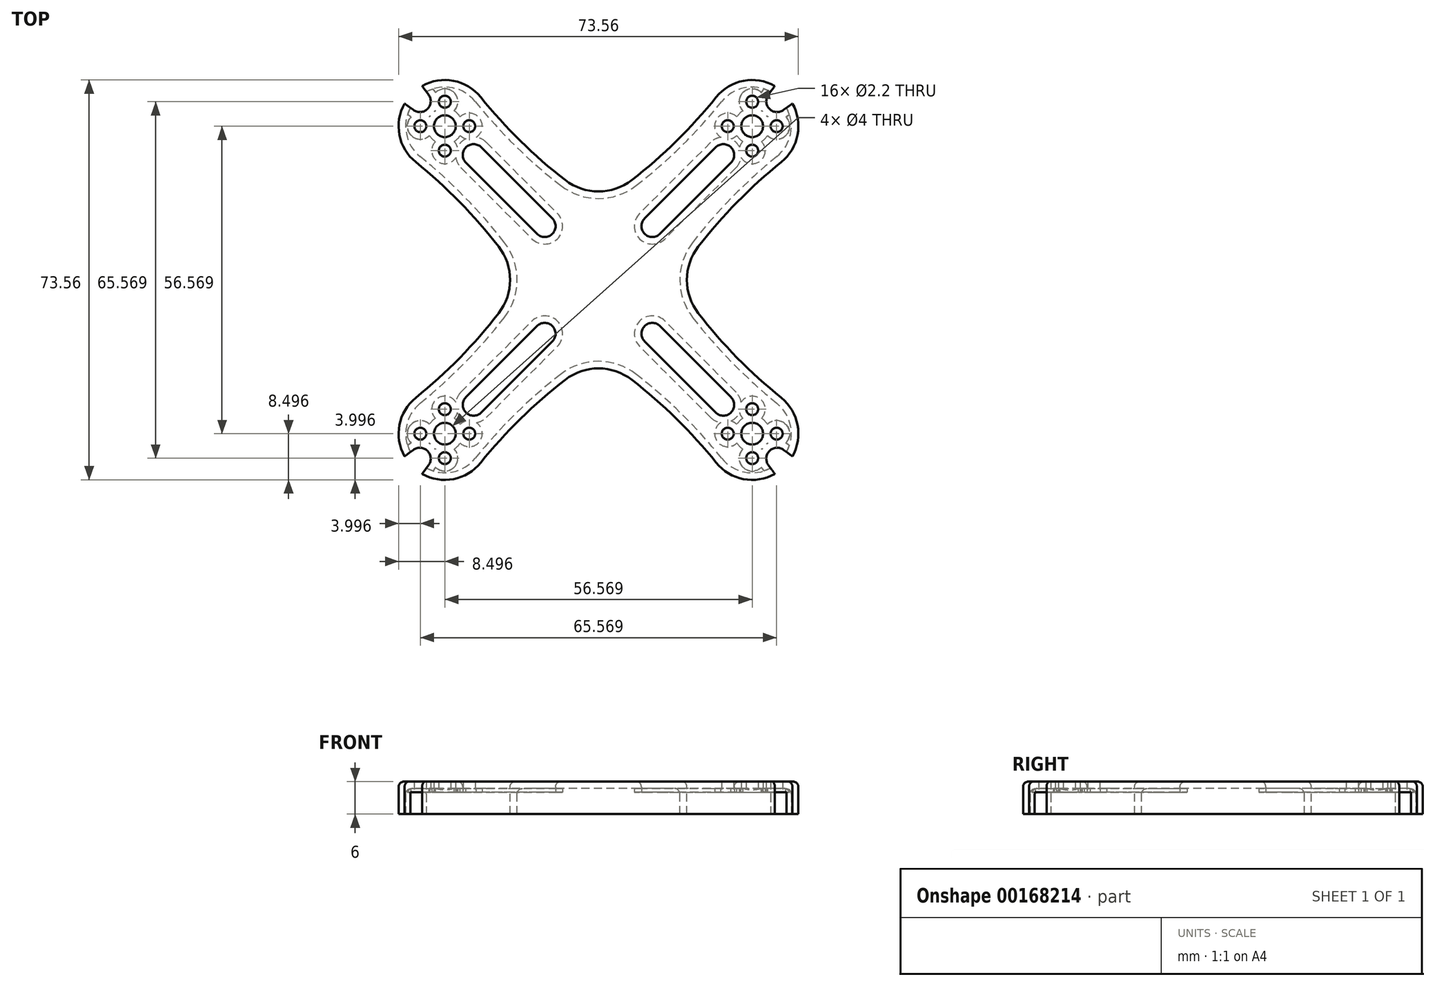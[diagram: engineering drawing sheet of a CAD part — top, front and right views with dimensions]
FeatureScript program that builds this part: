
annotation { "Feature Type Name" : "Feature", "Feature Type Description" : "" }
export const myFeature = defineFeature(function(context is Context, id is Id, definition is map)
    precondition{}
    {
        {
            var Q0;
            Q0=qCreatedBy(makeId("Top.planeOp"),FACE);
            var sketch = newSketch(context, id + "F0", { "sketchPlane" : qUnion([Q0])});
            skCircle(sketch, "E0", {"center": v(0, 0) * mm, "radius": 40 * mm, "construction": true});
            skLineSegment(sketch, "E1", {"start": v(0, 0) * mm, "end": v(-34.3, 34.3) * mm, "construction": true});
            skCircle(sketch, "E2", {"center": v(-28.28, 28.28) * mm, "radius": 2 * mm});
            skLineSegment(sketch, "E3", {"start": v(-28.28, 28.28) * mm, "end": v(-23.78, 28.28) * mm, "construction": true});
            skCircle(sketch, "E4", {"center": v(-23.78, 28.28) * mm, "radius": 1.1 * mm});
            skCircle(sketch, "E5.1.0", {"center": v(-28.28, 32.78) * mm, "radius": 1.1 * mm});
            skCircle(sketch, "E5.2.0", {"center": v(-32.78, 28.28) * mm, "radius": 1.1 * mm});
            skCircle(sketch, "E5.3.0", {"center": v(-28.28, 23.78) * mm, "radius": 1.1 * mm});
            skCircle(sketch, "E6", {"center": v(-28.28, 28.28) * mm, "radius": 7.5 * mm, "construction": true});
            skArc(sketch, "E7", {"start": v(-21.67, 33.62) * mm, "mid": v(-26.68, 36.63) * mm, "end": v(-32.46, 35.7) * mm});
            skCircle(sketch, "E8", {"center": v(-28.28, 28.28) * mm, "radius": 6.5 * mm, "construction": true});
            skCircle(sketch, "E9", {"center": v(0, 0) * mm, "radius": 6.5 * mm});
            skLineSegment(sketch, "E10", {"start": v(-28.28, 28.28) * mm, "end": v(-26.87, 29.7) * mm, "construction": true});
            skLineSegment(sketch, "E11", {"start": v(-23.69, 32.88) * mm, "end": v(4.6, 4.6) * mm, "construction": true});
            skLineSegment(sketch, "E12.MirrorCS", {"start": v(-32.88, 23.69) * mm, "end": v(-4.6, -4.6) * mm, "construction": true});
            skCircle(sketch, "E13", {"center": v(-28.28, 28.28) * mm, "radius": 26 * mm, "construction": true});
            skCircle(sketch, "E14", {"center": v(0, 0) * mm, "radius": 14 * mm});
            skArc(sketch, "E15", {"start": v(-21.67, 33.62) * mm, "mid": v(-11.6, 22.96) * mm, "end": v(0, 14) * mm});
            skArc(sketch, "E16.MirrorCS", {"start": v(-33.62, 21.67) * mm, "mid": v(-22.96, 11.6) * mm, "end": v(-14, 0) * mm});
            skLineSegment(sketch, "E17", {"start": v(-22.98, 22.98) * mm, "end": v(-9.9, 9.9) * mm});
            skArc(sketch, "E18.0.startCap", {"start": v(-24.4, 21.57) * mm, "mid": v(-24.4, 24.4) * mm, "end": v(-21.57, 24.4) * mm});
            skArc(sketch, "E18.0.endCap", {"start": v(-8.49, 11.31) * mm, "mid": v(-8.49, 8.49) * mm, "end": v(-11.31, 8.49) * mm});
            skLineSegment(sketch, "E18.0.left", {"start": v(-21.57, 24.4) * mm, "end": v(-8.49, 11.31) * mm});
            skLineSegment(sketch, "E18.0.right", {"start": v(-24.4, 21.57) * mm, "end": v(-11.31, 8.49) * mm});
            skArc(sketch, "E19", {"start": v(-34.06, 31.27) * mm, "mid": v(-31.47, 31.47) * mm, "end": v(-31.27, 34.06) * mm});
            skLineSegment(sketch, "E20", {"start": v(-31.27, 34.06) * mm, "end": v(-32.46, 35.7) * mm});
            skLineSegment(sketch, "E21.MirrorCS", {"start": v(-34.06, 31.27) * mm, "end": v(-35.7, 32.46) * mm});
            skArc(sketch, "E22.trimOffspring", {"start": v(-35.7, 32.46) * mm, "mid": v(-36.63, 26.68) * mm, "end": v(-33.62, 21.67) * mm});
            skLineSegment(sketch, "E23", {"start": v(0, 0) * mm, "end": v(0, 14) * mm});
            skLineSegment(sketch, "E24", {"start": v(0, 0) * mm, "end": v(-14, 0) * mm});
            skSolve(sketch);
        }
        {
            var Q0;
            {var subQ0=sQuery(id+"F0.wireOp",EDGE,"E23");var subQ1=sQuery(id+"F0.wireOp",EDGE,"E9");var subQ2=makeQuery(id+"F0.imprint","INTERSECT",VERTEX,{"derivedFrom":[subQ1,subQ0]});Q0=makeQuery(id+"F0.imprint","IMPRINT",FACE,{"disambiguationData":[TD([[makeQuery(id+"F0.imprint","IMPRINT",EDGE,{"disambiguationData":[TD([[subQ2,-1.0]])],"derivedFrom":subQ1}),1.0]])]});}
            var Q1;
            Q1=makeQuery(id+"F0.imprint","IMPRINT",FACE,{"disambiguationData":[TD([[makeQuery(id+"F0.imprint","IMPRINT",EDGE,{"derivedFrom":sQuery(id+"F0.wireOp",EDGE,"E2")}),-1.0]])]});
            var Q2;
            {var subQ4=sQuery(id+"F0.wireOp",EDGE,"E23");var subQ5=sQuery(id+"F0.wireOp",EDGE,"E9");var subQ6=makeQuery(id+"F0.imprint","INTERSECT",VERTEX,{"derivedFrom":[subQ5,subQ4]});Q2=makeQuery(id+"F0.imprint","IMPRINT",FACE,{"disambiguationData":[TD([[makeQuery(id+"F0.imprint","IMPRINT",EDGE,{"disambiguationData":[TD([[subQ6,-1.0]])],"derivedFrom":subQ5}),-1.0]])]});}
            extrude(context, id + "F1", {"entities" : qUnion([Q0, Q1, Q2]), "depth" : 6 * mm});
        }
        {
            var Q0;
            Q0=makeQuery(id+"F1.opExtrude","SWEPT_BODY",BODY,{"disambiguationData":[OSD([sQuery(id+"F0.wireOp",EDGE,"E2"),sQuery(id+"F0.wireOp",EDGE,"E4"),sQuery(id+"F0.wireOp",EDGE,"E5.1.0"),sQuery(id+"F0.wireOp",EDGE,"E5.2.0"),sQuery(id+"F0.wireOp",EDGE,"E5.3.0"),sQuery(id+"F0.wireOp",EDGE,"E7"),sQuery(id+"F0.wireOp",EDGE,"E15"),sQuery(id+"F0.wireOp",EDGE,"E16.MirrorCS"),sQuery(id+"F0.wireOp",EDGE,"E18.0.startCap"),sQuery(id+"F0.wireOp",EDGE,"E18.0.endCap"),sQuery(id+"F0.wireOp",EDGE,"E18.0.left"),sQuery(id+"F0.wireOp",EDGE,"E18.0.right"),sQuery(id+"F0.wireOp",EDGE,"E19"),sQuery(id+"F0.wireOp",EDGE,"E20"),sQuery(id+"F0.wireOp",EDGE,"E21.MirrorCS"),sQuery(id+"F0.wireOp",EDGE,"E22.trimOffspring"),sQuery(id+"F0.wireOp",EDGE,"E23"),sQuery(id+"F0.wireOp",EDGE,"E24")])]});
            var Q1;
            Q1=makeQuery(id+"F1.opExtrude","SWEPT_EDGE",EDGE,{"disambiguationData":[OSD([sQuery(id+"F0.wireOp",EDGE,"E23"),sQuery(id+"F0.wireOp",EDGE,"E24")])]});
            circularPattern(context, id + "F2", {"entities" : qUnion([Q0]), "axis" : qUnion([Q1]), "angle" : 360 * degree, "instanceCount" : 4, "equalSpace" : true});
        }
        {
            var Q0;
            Q0=makeQuery(id+"F1.opExtrude","SWEPT_BODY",BODY,{"disambiguationData":[OSD([sQuery(id+"F0.wireOp",EDGE,"E2"),sQuery(id+"F0.wireOp",EDGE,"E4"),sQuery(id+"F0.wireOp",EDGE,"E5.1.0"),sQuery(id+"F0.wireOp",EDGE,"E5.2.0"),sQuery(id+"F0.wireOp",EDGE,"E5.3.0"),sQuery(id+"F0.wireOp",EDGE,"E7"),sQuery(id+"F0.wireOp",EDGE,"E15"),sQuery(id+"F0.wireOp",EDGE,"E16.MirrorCS"),sQuery(id+"F0.wireOp",EDGE,"E18.0.startCap"),sQuery(id+"F0.wireOp",EDGE,"E18.0.endCap"),sQuery(id+"F0.wireOp",EDGE,"E18.0.left"),sQuery(id+"F0.wireOp",EDGE,"E18.0.right"),sQuery(id+"F0.wireOp",EDGE,"E19"),sQuery(id+"F0.wireOp",EDGE,"E20"),sQuery(id+"F0.wireOp",EDGE,"E21.MirrorCS"),sQuery(id+"F0.wireOp",EDGE,"E22.trimOffspring"),sQuery(id+"F0.wireOp",EDGE,"E23"),sQuery(id+"F0.wireOp",EDGE,"E24")])]});
            var Q1;
            Q1=makeQuery(id+"F2.opPattern","COPY",BODY,{"derivedFrom":makeQuery(id+"F1.opExtrude","SWEPT_BODY",BODY,{"disambiguationData":[OSD([sQuery(id+"F0.wireOp",EDGE,"E2"),sQuery(id+"F0.wireOp",EDGE,"E4"),sQuery(id+"F0.wireOp",EDGE,"E5.1.0"),sQuery(id+"F0.wireOp",EDGE,"E5.2.0"),sQuery(id+"F0.wireOp",EDGE,"E5.3.0"),sQuery(id+"F0.wireOp",EDGE,"E7"),sQuery(id+"F0.wireOp",EDGE,"E15"),sQuery(id+"F0.wireOp",EDGE,"E16.MirrorCS"),sQuery(id+"F0.wireOp",EDGE,"E18.0.startCap"),sQuery(id+"F0.wireOp",EDGE,"E18.0.endCap"),sQuery(id+"F0.wireOp",EDGE,"E18.0.left"),sQuery(id+"F0.wireOp",EDGE,"E18.0.right"),sQuery(id+"F0.wireOp",EDGE,"E19"),sQuery(id+"F0.wireOp",EDGE,"E20"),sQuery(id+"F0.wireOp",EDGE,"E21.MirrorCS"),sQuery(id+"F0.wireOp",EDGE,"E22.trimOffspring"),sQuery(id+"F0.wireOp",EDGE,"E23"),sQuery(id+"F0.wireOp",EDGE,"E24")])]}),"instanceName":"1"});
            var Q2;
            Q2=makeQuery(id+"F2.opPattern","COPY",BODY,{"derivedFrom":makeQuery(id+"F1.opExtrude","SWEPT_BODY",BODY,{"disambiguationData":[OSD([sQuery(id+"F0.wireOp",EDGE,"E2"),sQuery(id+"F0.wireOp",EDGE,"E4"),sQuery(id+"F0.wireOp",EDGE,"E5.1.0"),sQuery(id+"F0.wireOp",EDGE,"E5.2.0"),sQuery(id+"F0.wireOp",EDGE,"E5.3.0"),sQuery(id+"F0.wireOp",EDGE,"E7"),sQuery(id+"F0.wireOp",EDGE,"E15"),sQuery(id+"F0.wireOp",EDGE,"E16.MirrorCS"),sQuery(id+"F0.wireOp",EDGE,"E18.0.startCap"),sQuery(id+"F0.wireOp",EDGE,"E18.0.endCap"),sQuery(id+"F0.wireOp",EDGE,"E18.0.left"),sQuery(id+"F0.wireOp",EDGE,"E18.0.right"),sQuery(id+"F0.wireOp",EDGE,"E19"),sQuery(id+"F0.wireOp",EDGE,"E20"),sQuery(id+"F0.wireOp",EDGE,"E21.MirrorCS"),sQuery(id+"F0.wireOp",EDGE,"E22.trimOffspring"),sQuery(id+"F0.wireOp",EDGE,"E23"),sQuery(id+"F0.wireOp",EDGE,"E24")])]}),"instanceName":"2"});
            var Q3;
            Q3=makeQuery(id+"F2.opPattern","COPY",BODY,{"derivedFrom":makeQuery(id+"F1.opExtrude","SWEPT_BODY",BODY,{"disambiguationData":[OSD([sQuery(id+"F0.wireOp",EDGE,"E2"),sQuery(id+"F0.wireOp",EDGE,"E4"),sQuery(id+"F0.wireOp",EDGE,"E5.1.0"),sQuery(id+"F0.wireOp",EDGE,"E5.2.0"),sQuery(id+"F0.wireOp",EDGE,"E5.3.0"),sQuery(id+"F0.wireOp",EDGE,"E7"),sQuery(id+"F0.wireOp",EDGE,"E15"),sQuery(id+"F0.wireOp",EDGE,"E16.MirrorCS"),sQuery(id+"F0.wireOp",EDGE,"E18.0.startCap"),sQuery(id+"F0.wireOp",EDGE,"E18.0.endCap"),sQuery(id+"F0.wireOp",EDGE,"E18.0.left"),sQuery(id+"F0.wireOp",EDGE,"E18.0.right"),sQuery(id+"F0.wireOp",EDGE,"E19"),sQuery(id+"F0.wireOp",EDGE,"E20"),sQuery(id+"F0.wireOp",EDGE,"E21.MirrorCS"),sQuery(id+"F0.wireOp",EDGE,"E22.trimOffspring"),sQuery(id+"F0.wireOp",EDGE,"E23"),sQuery(id+"F0.wireOp",EDGE,"E24")])]}),"instanceName":"3"});
            booleanBodies(context, id + "F3", {"operationType" : BooleanOperationType.UNION, "tools" : qUnion([Q0, Q1, Q2, Q3])});
        }
        {
            var Q0;
            {var subQ0=sQuery(id+"F0.wireOp",EDGE,"E14");Q0=makeQuery(id+"F3.opBoolean","MERGE",EDGE,{"derivedFrom":[makeQuery(id+"F2.opPattern","COPY",EDGE,{"derivedFrom":makeQuery(id+"F1.opExtrude","SWEPT_EDGE",EDGE,{"disambiguationData":[OSD([subQ0,sQuery(id+"F0.wireOp",EDGE,"E15"),sQuery(id+"F0.wireOp",EDGE,"E23")])]}),"instanceName":"2"}),makeQuery(id+"F2.opPattern","COPY",EDGE,{"derivedFrom":makeQuery(id+"F1.opExtrude","SWEPT_EDGE",EDGE,{"disambiguationData":[OSD([subQ0,sQuery(id+"F0.wireOp",EDGE,"E16.MirrorCS"),sQuery(id+"F0.wireOp",EDGE,"E24")])]}),"instanceName":"3"})]});}
            var Q1;
            {var subQ0=sQuery(id+"F0.wireOp",EDGE,"E14");Q1=makeQuery(id+"F3.opBoolean","MERGE",EDGE,{"derivedFrom":[makeQuery(id+"F1.opExtrude","SWEPT_EDGE",EDGE,{"disambiguationData":[OSD([subQ0,sQuery(id+"F0.wireOp",EDGE,"E16.MirrorCS"),sQuery(id+"F0.wireOp",EDGE,"E24")])]}),makeQuery(id+"F2.opPattern","COPY",EDGE,{"derivedFrom":makeQuery(id+"F1.opExtrude","SWEPT_EDGE",EDGE,{"disambiguationData":[OSD([subQ0,sQuery(id+"F0.wireOp",EDGE,"E15"),sQuery(id+"F0.wireOp",EDGE,"E23")])]}),"instanceName":"3"})]});}
            var Q2;
            {var subQ0=sQuery(id+"F0.wireOp",EDGE,"E14");Q2=makeQuery(id+"F3.opBoolean","MERGE",EDGE,{"derivedFrom":[makeQuery(id+"F1.opExtrude","SWEPT_EDGE",EDGE,{"disambiguationData":[OSD([subQ0,sQuery(id+"F0.wireOp",EDGE,"E15"),sQuery(id+"F0.wireOp",EDGE,"E23")])]}),makeQuery(id+"F2.opPattern","COPY",EDGE,{"derivedFrom":makeQuery(id+"F1.opExtrude","SWEPT_EDGE",EDGE,{"disambiguationData":[OSD([subQ0,sQuery(id+"F0.wireOp",EDGE,"E16.MirrorCS"),sQuery(id+"F0.wireOp",EDGE,"E24")])]}),"instanceName":"1"})]});}
            var Q3;
            {var subQ0=sQuery(id+"F0.wireOp",EDGE,"E14");Q3=makeQuery(id+"F3.opBoolean","MERGE",EDGE,{"derivedFrom":[makeQuery(id+"F2.opPattern","COPY",EDGE,{"derivedFrom":makeQuery(id+"F1.opExtrude","SWEPT_EDGE",EDGE,{"disambiguationData":[OSD([subQ0,sQuery(id+"F0.wireOp",EDGE,"E15"),sQuery(id+"F0.wireOp",EDGE,"E23")])]}),"instanceName":"1"}),makeQuery(id+"F2.opPattern","COPY",EDGE,{"derivedFrom":makeQuery(id+"F1.opExtrude","SWEPT_EDGE",EDGE,{"disambiguationData":[OSD([subQ0,sQuery(id+"F0.wireOp",EDGE,"E16.MirrorCS"),sQuery(id+"F0.wireOp",EDGE,"E24")])]}),"instanceName":"2"})]});}
            fillet(context, id + "F4", {"entities" : qUnion([Q0, Q1, Q2, Q3]), "radius" : 10 * mm, "tangentPropagation" : true, "allowEdgeOverflow" : false});
        }
        {
            var Q0;
            {var subQ0=makeQuery(id+"F1.opExtrude","CAP_FACE",FACE,{"disambiguationData":[OSD([sQuery(id+"F0.wireOp",EDGE,"E2"),sQuery(id+"F0.wireOp",EDGE,"E4"),sQuery(id+"F0.wireOp",EDGE,"E5.1.0"),sQuery(id+"F0.wireOp",EDGE,"E5.2.0"),sQuery(id+"F0.wireOp",EDGE,"E5.3.0"),sQuery(id+"F0.wireOp",EDGE,"E7"),sQuery(id+"F0.wireOp",EDGE,"E15"),sQuery(id+"F0.wireOp",EDGE,"E16.MirrorCS"),sQuery(id+"F0.wireOp",EDGE,"E18.0.startCap"),sQuery(id+"F0.wireOp",EDGE,"E18.0.endCap"),sQuery(id+"F0.wireOp",EDGE,"E18.0.left"),sQuery(id+"F0.wireOp",EDGE,"E18.0.right"),sQuery(id+"F0.wireOp",EDGE,"E19"),sQuery(id+"F0.wireOp",EDGE,"E20"),sQuery(id+"F0.wireOp",EDGE,"E21.MirrorCS"),sQuery(id+"F0.wireOp",EDGE,"E22.trimOffspring"),sQuery(id+"F0.wireOp",EDGE,"E23"),sQuery(id+"F0.wireOp",EDGE,"E24")])],"isStart":true});Q0=makeQuery(id+"F3.opBoolean","MERGE",FACE,{"derivedFrom":[subQ0,makeQuery(id+"F2.opPattern","COPY",FACE,{"derivedFrom":subQ0,"instanceName":"1"}),makeQuery(id+"F2.opPattern","COPY",FACE,{"derivedFrom":subQ0,"instanceName":"2"}),makeQuery(id+"F2.opPattern","COPY",FACE,{"derivedFrom":subQ0,"instanceName":"3"})]});}
            shell(context, id + "F5", {"entities" : qUnion([Q0]), "thickness" : 1.3 * mm});
        }
        {
            var Q0;
            {var subQ0=makeQuery(id+"F1.opExtrude","CAP_FACE",FACE,{"disambiguationData":[OSD([sQuery(id+"F0.wireOp",EDGE,"E2"),sQuery(id+"F0.wireOp",EDGE,"E4"),sQuery(id+"F0.wireOp",EDGE,"E5.1.0"),sQuery(id+"F0.wireOp",EDGE,"E5.2.0"),sQuery(id+"F0.wireOp",EDGE,"E5.3.0"),sQuery(id+"F0.wireOp",EDGE,"E7"),sQuery(id+"F0.wireOp",EDGE,"E15"),sQuery(id+"F0.wireOp",EDGE,"E16.MirrorCS"),sQuery(id+"F0.wireOp",EDGE,"E18.0.startCap"),sQuery(id+"F0.wireOp",EDGE,"E18.0.endCap"),sQuery(id+"F0.wireOp",EDGE,"E18.0.left"),sQuery(id+"F0.wireOp",EDGE,"E18.0.right"),sQuery(id+"F0.wireOp",EDGE,"E19"),sQuery(id+"F0.wireOp",EDGE,"E20"),sQuery(id+"F0.wireOp",EDGE,"E21.MirrorCS"),sQuery(id+"F0.wireOp",EDGE,"E22.trimOffspring"),sQuery(id+"F0.wireOp",EDGE,"E23"),sQuery(id+"F0.wireOp",EDGE,"E24")])],"isStart":true});Q0=makeQuery(id+"F3.opBoolean","MERGE",FACE,{"derivedFrom":[subQ0,makeQuery(id+"F2.opPattern","COPY",FACE,{"derivedFrom":subQ0,"instanceName":"1"}),makeQuery(id+"F2.opPattern","COPY",FACE,{"derivedFrom":subQ0,"instanceName":"2"}),makeQuery(id+"F2.opPattern","COPY",FACE,{"derivedFrom":subQ0,"instanceName":"3"})]});}
            var sketch = newSketch(context, id + "F6", { "sketchPlane" : qUnion([Q0])});
            skPoint(sketch, "E25.0", {"position": v(21.5, 25.93) * mm});
            skLineSegment(sketch, "E26.0", {"start": v(25.31, 20.65) * mm, "end": v(12.23, 7.57) * mm});
            skArc(sketch, "E27.0", {"start": v(25.31, 20.65) * mm, "mid": v(25.93, 21.5) * mm, "end": v(26.25, 22.51) * mm});
            skArc(sketch, "E28.0", {"start": v(30, 25.46) * mm, "mid": v(29.77, 21.9) * mm, "end": v(26.25, 22.51) * mm});
            skArc(sketch, "E29.0", {"start": v(22.51, 26.25) * mm, "mid": v(21.5, 25.93) * mm, "end": v(20.65, 25.31) * mm});
            skLineSegment(sketch, "E30.0", {"start": v(20.65, 25.31) * mm, "end": v(7.57, 12.23) * mm});
            skArc(sketch, "E31.0", {"start": v(7.57, 12.23) * mm, "mid": v(7.57, 7.57) * mm, "end": v(12.23, 7.57) * mm});
            skArc(sketch, "E32.0", {"start": v(22.51, 26.25) * mm, "mid": v(21.9, 29.77) * mm, "end": v(25.46, 30) * mm});
            skArc(sketch, "E33.0", {"start": v(26.57, 31.1) * mm, "mid": v(26.6, 34.5) * mm, "end": v(29.99, 34.47) * mm});
            skArc(sketch, "E34.0", {"start": v(25.46, 30) * mm, "mid": v(25.95, 30.62) * mm, "end": v(26.57, 31.1) * mm});
            skArc(sketch, "E35.0", {"start": v(31.1, 26.57) * mm, "mid": v(30.62, 25.95) * mm, "end": v(30, 25.46) * mm});
            skArc(sketch, "E36.0", {"start": v(34.47, 29.99) * mm, "mid": v(34.5, 26.6) * mm, "end": v(31.1, 26.57) * mm});
            skArc(sketch, "E37.0", {"start": v(34.83, 30.22) * mm, "mid": v(34.65, 30.1) * mm, "end": v(34.47, 29.99) * mm});
            skLineSegment(sketch, "E38.0", {"start": v(34.83, 30.22) * mm, "end": v(35.15, 30.45) * mm});
            skArc(sketch, "E39.0", {"start": v(29.99, 34.47) * mm, "mid": v(30.1, 34.65) * mm, "end": v(30.22, 34.83) * mm});
            skLineSegment(sketch, "E40.0", {"start": v(30.22, 34.83) * mm, "end": v(30.45, 35.15) * mm});
            skArc(sketch, "E41", {"start": v(35.15, 30.45) * mm, "mid": v(33.38, 33.38) * mm, "end": v(30.45, 35.15) * mm});
            skArc(sketch, "E42.MirrorCS", {"start": v(-34.83, 30.22) * mm, "mid": v(-34.65, 30.1) * mm, "end": v(-34.47, 29.99) * mm});
            skLineSegment(sketch, "E43.MirrorCS", {"start": v(-34.83, 30.22) * mm, "end": v(-35.15, 30.45) * mm});
            skArc(sketch, "E44.MirrorCS", {"start": v(-29.99, 34.47) * mm, "mid": v(-30.1, 34.65) * mm, "end": v(-30.22, 34.83) * mm});
            skArc(sketch, "E45.MirrorCS", {"start": v(-31.1, 26.57) * mm, "mid": v(-30.62, 25.95) * mm, "end": v(-30, 25.46) * mm});
            skArc(sketch, "E46.MirrorCS", {"start": v(-22.51, 26.25) * mm, "mid": v(-21.5, 25.93) * mm, "end": v(-20.65, 25.31) * mm});
            skArc(sketch, "E47.MirrorCS", {"start": v(-25.31, 20.65) * mm, "mid": v(-25.93, 21.5) * mm, "end": v(-26.25, 22.51) * mm});
            skLineSegment(sketch, "E48.MirrorCS", {"start": v(-30.22, 34.83) * mm, "end": v(-30.45, 35.15) * mm});
            skArc(sketch, "E49.MirrorCS", {"start": v(-25.46, 30) * mm, "mid": v(-25.95, 30.62) * mm, "end": v(-26.57, 31.1) * mm});
            skArc(sketch, "E50.MirrorCS", {"start": v(-34.47, 29.99) * mm, "mid": v(-34.5, 26.6) * mm, "end": v(-31.1, 26.57) * mm});
            skArc(sketch, "E51.MirrorCS", {"start": v(-26.57, 31.1) * mm, "mid": v(-26.6, 34.5) * mm, "end": v(-29.99, 34.47) * mm});
            skArc(sketch, "E52.MirrorCS", {"start": v(-22.51, 26.25) * mm, "mid": v(-21.9, 29.77) * mm, "end": v(-25.46, 30) * mm});
            skLineSegment(sketch, "E53.MirrorCS", {"start": v(-20.65, 25.31) * mm, "end": v(-7.57, 12.23) * mm});
            skArc(sketch, "E54.MirrorCS", {"start": v(-30, 25.46) * mm, "mid": v(-29.77, 21.9) * mm, "end": v(-26.25, 22.51) * mm});
            skPoint(sketch, "E55.MirrorP", {"position": v(-21.5, 25.93) * mm});
            skLineSegment(sketch, "E56.MirrorCS", {"start": v(-25.31, 20.65) * mm, "end": v(-12.23, 7.57) * mm});
            skArc(sketch, "E57.MirrorCS", {"start": v(-35.15, 30.45) * mm, "mid": v(-33.38, 33.38) * mm, "end": v(-30.45, 35.15) * mm});
            skArc(sketch, "E58.MirrorCS", {"start": v(-7.57, 12.23) * mm, "mid": v(-7.57, 7.57) * mm, "end": v(-12.23, 7.57) * mm});
            skArc(sketch, "E59.MirrorCS", {"start": v(-34.83, -30.22) * mm, "mid": v(-34.65, -30.1) * mm, "end": v(-34.47, -29.99) * mm});
            skLineSegment(sketch, "E60.MirrorCS", {"start": v(-34.83, -30.22) * mm, "end": v(-35.15, -30.45) * mm});
            skArc(sketch, "E61.MirrorCS", {"start": v(34.83, -30.22) * mm, "mid": v(34.65, -30.1) * mm, "end": v(34.47, -29.99) * mm});
            skLineSegment(sketch, "E62.MirrorCS", {"start": v(34.83, -30.22) * mm, "end": v(35.15, -30.45) * mm});
            skArc(sketch, "E63.MirrorCS", {"start": v(-29.99, -34.47) * mm, "mid": v(-30.1, -34.65) * mm, "end": v(-30.22, -34.83) * mm});
            skLineSegment(sketch, "E64.MirrorCS", {"start": v(30.22, -34.83) * mm, "end": v(30.45, -35.15) * mm});
            skArc(sketch, "E65.MirrorCS", {"start": v(29.99, -34.47) * mm, "mid": v(30.1, -34.65) * mm, "end": v(30.22, -34.83) * mm});
            skLineSegment(sketch, "E66.MirrorCS", {"start": v(-30.22, -34.83) * mm, "end": v(-30.45, -35.15) * mm});
            skArc(sketch, "E67.MirrorCS", {"start": v(22.51, -26.25) * mm, "mid": v(21.5, -25.93) * mm, "end": v(20.65, -25.31) * mm});
            skArc(sketch, "E68.MirrorCS", {"start": v(-22.51, -26.25) * mm, "mid": v(-21.5, -25.93) * mm, "end": v(-20.65, -25.31) * mm});
            skArc(sketch, "E69.MirrorCS", {"start": v(25.46, -30) * mm, "mid": v(25.95, -30.62) * mm, "end": v(26.57, -31.1) * mm});
            skArc(sketch, "E70.MirrorCS", {"start": v(31.1, -26.57) * mm, "mid": v(30.62, -25.95) * mm, "end": v(30, -25.46) * mm});
            skArc(sketch, "E71.MirrorCS", {"start": v(-25.46, -30) * mm, "mid": v(-25.95, -30.62) * mm, "end": v(-26.57, -31.1) * mm});
            skArc(sketch, "E72.MirrorCS", {"start": v(-31.1, -26.57) * mm, "mid": v(-30.62, -25.95) * mm, "end": v(-30, -25.46) * mm});
            skArc(sketch, "E73.MirrorCS", {"start": v(25.31, -20.65) * mm, "mid": v(25.93, -21.5) * mm, "end": v(26.25, -22.51) * mm});
            skArc(sketch, "E74.MirrorCS", {"start": v(35.15, -30.45) * mm, "mid": v(33.38, -33.38) * mm, "end": v(30.45, -35.15) * mm});
            skArc(sketch, "E75.MirrorCS", {"start": v(-35.15, -30.45) * mm, "mid": v(-33.38, -33.38) * mm, "end": v(-30.45, -35.15) * mm});
            skArc(sketch, "E76.MirrorCS", {"start": v(-25.31, -20.65) * mm, "mid": v(-25.93, -21.5) * mm, "end": v(-26.25, -22.51) * mm});
            skArc(sketch, "E77.MirrorCS", {"start": v(26.57, -31.1) * mm, "mid": v(26.6, -34.5) * mm, "end": v(29.99, -34.47) * mm});
            skArc(sketch, "E78.MirrorCS", {"start": v(34.47, -29.99) * mm, "mid": v(34.5, -26.6) * mm, "end": v(31.1, -26.57) * mm});
            skPoint(sketch, "E79.MirrorP", {"position": v(-21.5, -25.93) * mm});
            skPoint(sketch, "E80.MirrorP", {"position": v(21.5, -25.93) * mm});
            skArc(sketch, "E81.MirrorCS", {"start": v(-34.47, -29.99) * mm, "mid": v(-34.5, -26.6) * mm, "end": v(-31.1, -26.57) * mm});
            skArc(sketch, "E82.MirrorCS", {"start": v(-26.57, -31.1) * mm, "mid": v(-26.6, -34.5) * mm, "end": v(-29.99, -34.47) * mm});
            skArc(sketch, "E83.MirrorCS", {"start": v(22.51, -26.25) * mm, "mid": v(21.9, -29.77) * mm, "end": v(25.46, -30) * mm});
            skArc(sketch, "E84.MirrorCS", {"start": v(7.57, -12.23) * mm, "mid": v(7.57, -7.57) * mm, "end": v(12.23, -7.57) * mm});
            skLineSegment(sketch, "E85.MirrorCS", {"start": v(20.65, -25.31) * mm, "end": v(7.57, -12.23) * mm});
            skArc(sketch, "E86.MirrorCS", {"start": v(-22.51, -26.25) * mm, "mid": v(-21.9, -29.77) * mm, "end": v(-25.46, -30) * mm});
            skArc(sketch, "E87.MirrorCS", {"start": v(30, -25.46) * mm, "mid": v(29.77, -21.9) * mm, "end": v(26.25, -22.51) * mm});
            skLineSegment(sketch, "E88.MirrorCS", {"start": v(25.31, -20.65) * mm, "end": v(12.23, -7.57) * mm});
            skArc(sketch, "E89.MirrorCS", {"start": v(-7.57, -12.23) * mm, "mid": v(-7.57, -7.57) * mm, "end": v(-12.23, -7.57) * mm});
            skLineSegment(sketch, "E90.MirrorCS", {"start": v(-20.65, -25.31) * mm, "end": v(-7.57, -12.23) * mm});
            skLineSegment(sketch, "E91.MirrorCS", {"start": v(-25.31, -20.65) * mm, "end": v(-12.23, -7.57) * mm});
            skArc(sketch, "E92.MirrorCS", {"start": v(-30, -25.46) * mm, "mid": v(-29.77, -21.9) * mm, "end": v(-26.25, -22.51) * mm});
            skSolve(sketch);
        }
        {
            var Q0;
            Q0 = qSketchRegion(id + "F6", true);
            extrude(context, id + "F7", {"entities" : qUnion([Q0]), "operationType" : NewBodyOperationType.REMOVE, "oppositeDirection" : true, "depth" : 4 * mm});
        }
        {
            var Q0;
            {var subQ0=sQuery(id+"F0.wireOp",EDGE,"E22.trimOffspring");Q0=makeQuery(id+"F5.opShell","OFFSET_EDGE",EDGE,{"disambiguationData":[OSD([subQ0]),TDD([makeQuery(id+"F2.opPattern","COPY",EDGE,{"derivedFrom":makeQuery(id+"F1.opExtrude","CAP_EDGE",EDGE,{"disambiguationData":[OSD([subQ0])],"isStart":false}),"instanceName":"3"})])]});}
            var Q1;
            {var subQ0=sQuery(id+"F0.wireOp",EDGE,"E16.MirrorCS");Q1=makeQuery(id+"F5.opShell","OFFSET_EDGE",EDGE,{"disambiguationData":[OSD([subQ0]),TDD([makeQuery(id+"F2.opPattern","COPY",EDGE,{"derivedFrom":makeQuery(id+"F1.opExtrude","CAP_EDGE",EDGE,{"disambiguationData":[OSD([subQ0])],"isStart":false}),"instanceName":"3"})])]});}
            var Q2;
            {var subQ0=sQuery(id+"F0.wireOp",EDGE,"E24");var subQ1=sQuery(id+"F0.wireOp",EDGE,"E23");var subQ2=sQuery(id+"F0.wireOp",EDGE,"E22.trimOffspring");var subQ3=sQuery(id+"F0.wireOp",EDGE,"E21.MirrorCS");var subQ4=sQuery(id+"F0.wireOp",EDGE,"E20");var subQ5=sQuery(id+"F0.wireOp",EDGE,"E19");var subQ6=sQuery(id+"F0.wireOp",EDGE,"E18.0.right");var subQ7=sQuery(id+"F0.wireOp",EDGE,"E18.0.left");var subQ8=sQuery(id+"F0.wireOp",EDGE,"E18.0.endCap");var subQ9=sQuery(id+"F0.wireOp",EDGE,"E18.0.startCap");var subQ10=sQuery(id+"F0.wireOp",EDGE,"E16.MirrorCS");var subQ11=sQuery(id+"F0.wireOp",EDGE,"E15");var subQ12=sQuery(id+"F0.wireOp",EDGE,"E7");var subQ13=sQuery(id+"F0.wireOp",EDGE,"E5.3.0");var subQ14=sQuery(id+"F0.wireOp",EDGE,"E5.2.0");var subQ15=sQuery(id+"F0.wireOp",EDGE,"E5.1.0");var subQ16=sQuery(id+"F0.wireOp",EDGE,"E4");var subQ17=sQuery(id+"F0.wireOp",EDGE,"E2");var subQ18=makeQuery(id+"F1.opExtrude","CAP_FACE",FACE,{"disambiguationData":[OSD([subQ17,subQ16,subQ15,subQ14,subQ13,subQ12,subQ11,subQ10,subQ9,subQ8,subQ7,subQ6,subQ5,subQ4,subQ3,subQ2,subQ1,subQ0])],"isStart":false});var subQ19=sQuery(id+"F0.wireOp",EDGE,"E14");Q2=makeQuery(id+"F5.opShell","OFFSET_EDGE",EDGE,{"disambiguationData":[OSD([subQ17,subQ16,subQ15,subQ14,subQ13,subQ12,subQ19,subQ11,subQ10,subQ9,subQ8,subQ7,subQ6,subQ5,subQ4,subQ3,subQ2,subQ1,subQ0]),TDD([makeQuery(id+"F4.opFillet","BLEND_EDGE",EDGE,{"blendedFrom":[makeQuery(id+"F3.opBoolean","MERGE",EDGE,{"derivedFrom":[makeQuery(id+"F2.opPattern","COPY",EDGE,{"derivedFrom":makeQuery(id+"F1.opExtrude","SWEPT_EDGE",EDGE,{"disambiguationData":[OSD([subQ19,subQ11,subQ1])]}),"instanceName":"2"}),makeQuery(id+"F2.opPattern","COPY",EDGE,{"derivedFrom":makeQuery(id+"F1.opExtrude","SWEPT_EDGE",EDGE,{"disambiguationData":[OSD([subQ19,subQ10,subQ0])]}),"instanceName":"3"})]}),makeQuery(id+"F3.opBoolean","MERGE",FACE,{"derivedFrom":[subQ18,makeQuery(id+"F2.opPattern","COPY",FACE,{"derivedFrom":subQ18,"instanceName":"1"}),makeQuery(id+"F2.opPattern","COPY",FACE,{"derivedFrom":subQ18,"instanceName":"2"}),makeQuery(id+"F2.opPattern","COPY",FACE,{"derivedFrom":subQ18,"instanceName":"3"})]})],"blendedInto":[makeQuery(id+"F3.opBoolean","MERGE",FACE,{"derivedFrom":[subQ18,makeQuery(id+"F2.opPattern","COPY",FACE,{"derivedFrom":subQ18,"instanceName":"1"}),makeQuery(id+"F2.opPattern","COPY",FACE,{"derivedFrom":subQ18,"instanceName":"2"}),makeQuery(id+"F2.opPattern","COPY",FACE,{"derivedFrom":subQ18,"instanceName":"3"})]})]})])]});}
            var Q3;
            {var subQ0=sQuery(id+"F0.wireOp",EDGE,"E16.MirrorCS");Q3=makeQuery(id+"F5.opShell","OFFSET_EDGE",EDGE,{"disambiguationData":[OSD([subQ0]),TDD([makeQuery(id+"F2.opPattern","COPY",EDGE,{"derivedFrom":makeQuery(id+"F1.opExtrude","CAP_EDGE",EDGE,{"disambiguationData":[OSD([subQ0])],"isStart":false}),"instanceName":"2"})])]});}
            var Q4;
            {var subQ0=sQuery(id+"F0.wireOp",EDGE,"E15");Q4=makeQuery(id+"F5.opShell","OFFSET_EDGE",EDGE,{"disambiguationData":[OSD([subQ0]),TDD([makeQuery(id+"F2.opPattern","COPY",EDGE,{"derivedFrom":makeQuery(id+"F1.opExtrude","CAP_EDGE",EDGE,{"disambiguationData":[OSD([subQ0])],"isStart":false}),"instanceName":"3"})])]});}
            var Q5;
            {var subQ0=sQuery(id+"F0.wireOp",EDGE,"E24");var subQ1=sQuery(id+"F0.wireOp",EDGE,"E23");var subQ2=sQuery(id+"F0.wireOp",EDGE,"E22.trimOffspring");var subQ3=sQuery(id+"F0.wireOp",EDGE,"E21.MirrorCS");var subQ4=sQuery(id+"F0.wireOp",EDGE,"E20");var subQ5=sQuery(id+"F0.wireOp",EDGE,"E19");var subQ6=sQuery(id+"F0.wireOp",EDGE,"E18.0.right");var subQ7=sQuery(id+"F0.wireOp",EDGE,"E18.0.left");var subQ8=sQuery(id+"F0.wireOp",EDGE,"E18.0.endCap");var subQ9=sQuery(id+"F0.wireOp",EDGE,"E18.0.startCap");var subQ10=sQuery(id+"F0.wireOp",EDGE,"E16.MirrorCS");var subQ11=sQuery(id+"F0.wireOp",EDGE,"E15");var subQ12=sQuery(id+"F0.wireOp",EDGE,"E7");var subQ13=sQuery(id+"F0.wireOp",EDGE,"E5.3.0");var subQ14=sQuery(id+"F0.wireOp",EDGE,"E5.2.0");var subQ15=sQuery(id+"F0.wireOp",EDGE,"E5.1.0");var subQ16=sQuery(id+"F0.wireOp",EDGE,"E4");var subQ17=sQuery(id+"F0.wireOp",EDGE,"E2");var subQ18=makeQuery(id+"F1.opExtrude","CAP_FACE",FACE,{"disambiguationData":[OSD([subQ17,subQ16,subQ15,subQ14,subQ13,subQ12,subQ11,subQ10,subQ9,subQ8,subQ7,subQ6,subQ5,subQ4,subQ3,subQ2,subQ1,subQ0])],"isStart":false});var subQ19=sQuery(id+"F0.wireOp",EDGE,"E14");Q5=makeQuery(id+"F5.opShell","OFFSET_EDGE",EDGE,{"disambiguationData":[OSD([subQ17,subQ16,subQ15,subQ14,subQ13,subQ12,subQ19,subQ11,subQ10,subQ9,subQ8,subQ7,subQ6,subQ5,subQ4,subQ3,subQ2,subQ1,subQ0]),TDD([makeQuery(id+"F4.opFillet","BLEND_EDGE",EDGE,{"blendedFrom":[makeQuery(id+"F3.opBoolean","MERGE",EDGE,{"derivedFrom":[makeQuery(id+"F1.opExtrude","SWEPT_EDGE",EDGE,{"disambiguationData":[OSD([subQ19,subQ11,subQ1])]}),makeQuery(id+"F2.opPattern","COPY",EDGE,{"derivedFrom":makeQuery(id+"F1.opExtrude","SWEPT_EDGE",EDGE,{"disambiguationData":[OSD([subQ19,subQ10,subQ0])]}),"instanceName":"1"})]}),makeQuery(id+"F3.opBoolean","MERGE",FACE,{"derivedFrom":[subQ18,makeQuery(id+"F2.opPattern","COPY",FACE,{"derivedFrom":subQ18,"instanceName":"1"}),makeQuery(id+"F2.opPattern","COPY",FACE,{"derivedFrom":subQ18,"instanceName":"2"}),makeQuery(id+"F2.opPattern","COPY",FACE,{"derivedFrom":subQ18,"instanceName":"3"})]})],"blendedInto":[makeQuery(id+"F3.opBoolean","MERGE",FACE,{"derivedFrom":[subQ18,makeQuery(id+"F2.opPattern","COPY",FACE,{"derivedFrom":subQ18,"instanceName":"1"}),makeQuery(id+"F2.opPattern","COPY",FACE,{"derivedFrom":subQ18,"instanceName":"2"}),makeQuery(id+"F2.opPattern","COPY",FACE,{"derivedFrom":subQ18,"instanceName":"3"})]})]})])]});}
            var Q6;
            Q6=makeQuery(id+"F2.opPattern","COPY",EDGE,{"derivedFrom":makeQuery(id+"F1.opExtrude","CAP_EDGE",EDGE,{"disambiguationData":[OSD([sQuery(id+"F0.wireOp",EDGE,"E15")])],"isStart":false}),"instanceName":"2"});
            var Q7;
            Q7=makeQuery(id+"F2.opPattern","COPY",EDGE,{"derivedFrom":makeQuery(id+"F1.opExtrude","CAP_EDGE",EDGE,{"disambiguationData":[OSD([sQuery(id+"F0.wireOp",EDGE,"E22.trimOffspring")])],"isStart":false}),"instanceName":"2"});
            var Q8;
            Q8=makeQuery(id+"F2.opPattern","COPY",EDGE,{"derivedFrom":makeQuery(id+"F1.opExtrude","CAP_EDGE",EDGE,{"disambiguationData":[OSD([sQuery(id+"F0.wireOp",EDGE,"E16.MirrorCS")])],"isStart":false}),"instanceName":"1"});
            var Q9;
            Q9=makeQuery(id+"F1.opExtrude","CAP_EDGE",EDGE,{"disambiguationData":[OSD([sQuery(id+"F0.wireOp",EDGE,"E16.MirrorCS")])],"isStart":false});
            var Q10;
            Q10=makeQuery(id+"F1.opExtrude","CAP_EDGE",EDGE,{"disambiguationData":[OSD([sQuery(id+"F0.wireOp",EDGE,"E18.0.left")])],"isStart":false});
            var Q11;
            Q11=makeQuery(id+"F2.opPattern","COPY",EDGE,{"derivedFrom":makeQuery(id+"F1.opExtrude","CAP_EDGE",EDGE,{"disambiguationData":[OSD([sQuery(id+"F0.wireOp",EDGE,"E18.0.right")])],"isStart":false}),"instanceName":"1"});
            var Q12;
            Q12=makeQuery(id+"F2.opPattern","COPY",EDGE,{"derivedFrom":makeQuery(id+"F1.opExtrude","CAP_EDGE",EDGE,{"disambiguationData":[OSD([sQuery(id+"F0.wireOp",EDGE,"E18.0.right")])],"isStart":false}),"instanceName":"2"});
            var Q13;
            Q13=makeQuery(id+"F2.opPattern","COPY",EDGE,{"derivedFrom":makeQuery(id+"F1.opExtrude","CAP_EDGE",EDGE,{"disambiguationData":[OSD([sQuery(id+"F0.wireOp",EDGE,"E18.0.left")])],"isStart":false}),"instanceName":"3"});
            fillet(context, id + "F8", {"entities" : qUnion([Q0, Q1, Q2, Q3, Q4, Q5, Q6, Q7, Q8, Q9, Q10, Q11, Q12, Q13]), "radius" : 1 * mm, "tangentPropagation" : true, "allowEdgeOverflow" : false});
        }
    });
